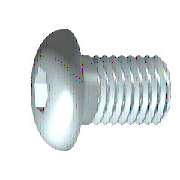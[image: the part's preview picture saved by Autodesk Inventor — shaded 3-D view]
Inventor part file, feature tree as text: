
AUTODESK INVENTOR PART (.ipt)
format: ipt  version: 2013 (Build 170138000, 138)  size: 199,680 bytes
history: native  units: mm (DEFAULTED — no unit token found)
features: sketch x2, extrude x1, plane x1, fillet x1
ambient origin geometry x7: Origin, YZ Plane, XY Plane, X Axis, Y Axis, Z Axis, Center Point
bodies: Solid1 (feature_tree), Body (feature_tree)
feature tree (5):
  extrude  "Slot"  Depth=1.59014mm
  plane  "Work Plane1"
  fillet  "Fillet2"  Radius=2.2098mm
  sketch  "Sketch1"  dims[d1=4.75976mm d2=1.59014mm d3=2.2098mm]
  sketch  "Sketch2"  dims[d4=1.3208mm d5=60.0deg d6=4.1656mm d7=4.1656mm d8=2.756963mm d9=7.9248mm d10=90.0deg d11=10.0mm d12=0.0mm d13=4.75976mm d14=0.0mm d15=0.486918mm d16=0.486918mm d17=1.9558mm d19=0.0mm d26=6.35mm d27=45.0deg d28=0.0mm d29=0.0mm d30=0.1mm]
